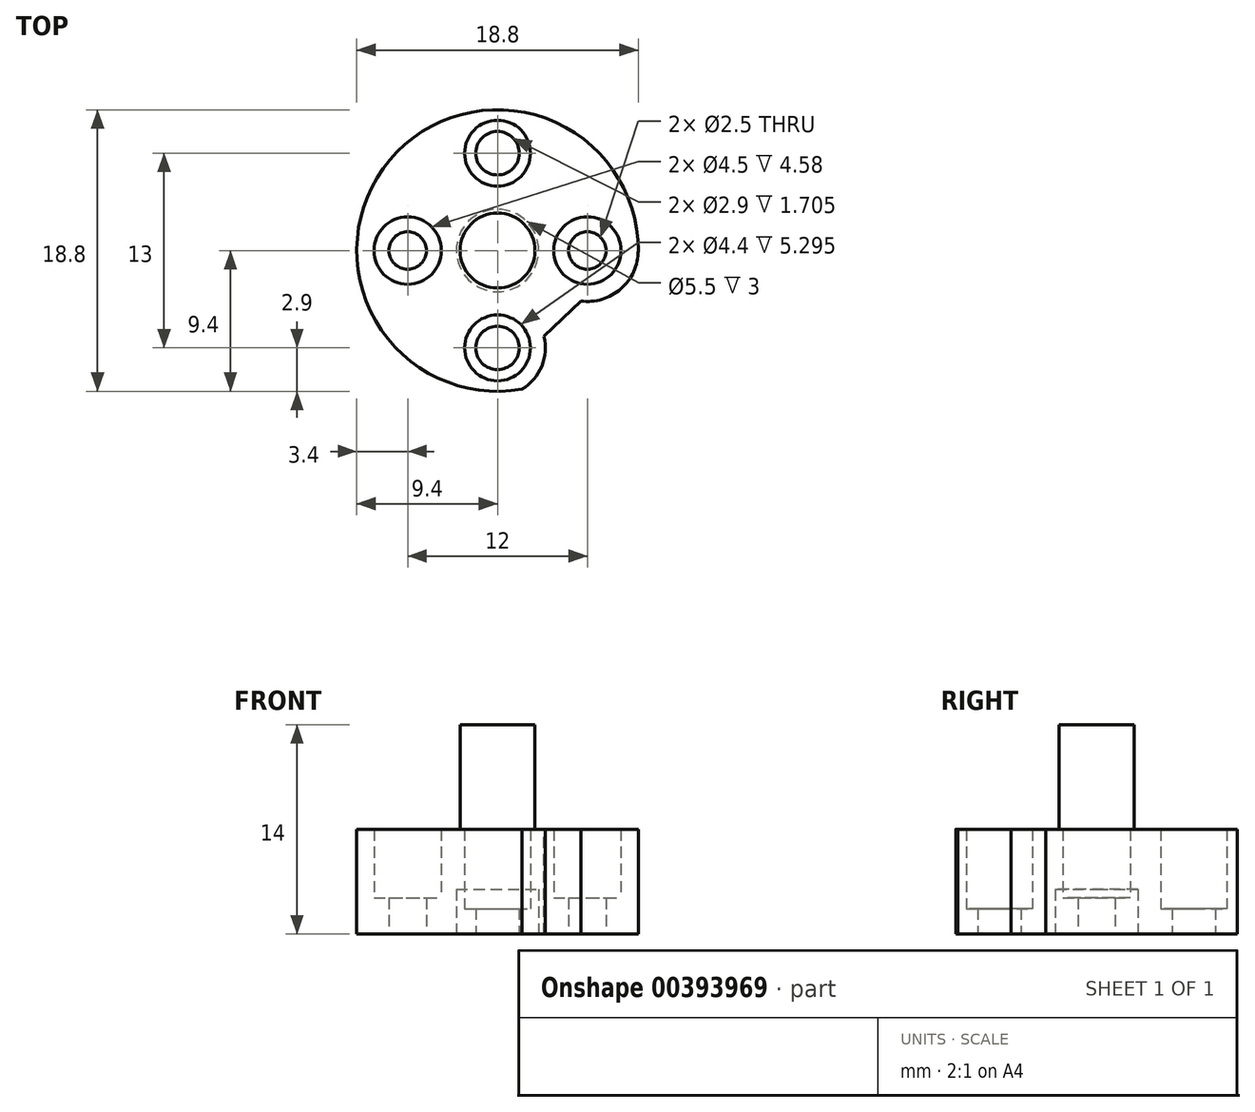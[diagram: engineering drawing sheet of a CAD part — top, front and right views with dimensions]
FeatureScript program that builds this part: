
annotation { "Feature Type Name" : "Feature", "Feature Type Description" : "" }
export const myFeature = defineFeature(function(context is Context, id is Id, definition is map)
    precondition{}
    {
        {
            var Q0;
            Q0=qCreatedBy(makeId("Top.planeOp"),FACE);
            var sketch = newSketch(context, id + "F0", { "sketchPlane" : qUnion([Q0])});
            skCircle(sketch, "E0", {"center": v(0, 0) * mm, "radius": 9.4 * mm});
            skSolve(sketch);
        }
        {
            var Q0;
            Q0 = qSketchRegion(id + "F0", true);
            extrude(context, id + "F1", {"entities" : qUnion([Q0]), "depth" : 7 * mm});
        }
        {
            var Q0;
            Q0=makeQuery(id+"F1.opExtrude","CAP_FACE",FACE,{"disambiguationData":[OSD([sQuery(id+"F0.wireOp",EDGE,"E0")])],"isStart":false});
            var sketch = newSketch(context, id + "F2", { "sketchPlane" : qUnion([Q0])});
            skCircle(sketch, "E1", {"center": v(0, 0) * mm, "radius": 2.5 * mm});
            skSolve(sketch);
        }
        {
            var Q0;
            Q0 = qSketchRegion(id + "F2", true);
            extrude(context, id + "F3", {"entities" : qUnion([Q0]), "operationType" : NewBodyOperationType.ADD, "depth" : 7 * mm});
        }
        {
            var Q0;
            Q0=makeQuery(id+"F1.opExtrude","CAP_FACE",FACE,{"disambiguationData":[OSD([sQuery(id+"F0.wireOp",EDGE,"E0")])],"isStart":true});
            var sketch = newSketch(context, id + "F4", { "sketchPlane" : qUnion([Q0])});
            skCircle(sketch, "E2", {"center": v(6, 0) * mm, "radius": 1.25 * mm});
            skLineSegment(sketch, "E3", {"start": v(0, 0) * mm, "end": v(6, 0) * mm, "construction": true});
            skCircle(sketch, "E4.MirrorC", {"center": v(-6, 0) * mm, "radius": 1.25 * mm});
            skSolve(sketch);
        }
        {
            var Q0;
            Q0 = qSketchRegion(id + "F4", true);
            extrude(context, id + "F5", {"entities" : qUnion([Q0]), "operationType" : NewBodyOperationType.REMOVE, "oppositeDirection" : true, "depth" : ((4.7 - 2.5) * 1.1) * mm});
        }
        {
            var Q0;
            Q0=makeQuery(id+"F5.boolean.opBoolean","COPY",FACE,{"derivedFrom":makeQuery(id+"F5.opExtrude","CAP_FACE",FACE,{"disambiguationData":[OSD([sQuery(id+"F4.wireOp",EDGE,"E4.MirrorC")])],"isStart":false})});
            var sketch = newSketch(context, id + "F6", { "sketchPlane" : qUnion([Q0])});
            skCircle(sketch, "E5", {"center": v(-6, 0) * mm, "radius": 2.25 * mm});
            skCircle(sketch, "E6.MirrorC", {"center": v(6, 0) * mm, "radius": 2.25 * mm});
            skSolve(sketch);
        }
        {
            var Q0;
            Q0 = qSketchRegion(id + "F6", true);
            var Q1;
            Q1=makeQuery(id+"F1.opExtrude","CAP_FACE",FACE,{"disambiguationData":[OSD([sQuery(id+"F0.wireOp",EDGE,"E0")])],"isStart":false});
            extrude(context, id + "F7", {"entities" : qUnion([Q0]), "operationType" : NewBodyOperationType.REMOVE, "endBound" : BoundingType.UP_TO_SURFACE, "oppositeDirection" : true, "endBoundEntityFace" : qUnion([Q1]), "depth" : 25 * mm});
        }
        {
            var Q0;
            Q0=makeQuery(id+"F1.opExtrude","CAP_FACE",FACE,{"disambiguationData":[OSD([sQuery(id+"F0.wireOp",EDGE,"E0")])],"isStart":true});
            var sketch = newSketch(context, id + "F8", { "sketchPlane" : qUnion([Q0])});
            skLineSegment(sketch, "E7", {"start": v(0, 0) * mm, "end": v(0, -6.5) * mm, "construction": true});
            skCircle(sketch, "E8", {"center": v(0, -6.5) * mm, "radius": 1.45 * mm});
            skCircle(sketch, "E9.MirrorC", {"center": v(0, 6.5) * mm, "radius": 1.45 * mm});
            skSolve(sketch);
        }
        {
            var Q0;
            Q0 = qSketchRegion(id + "F8", true);
            extrude(context, id + "F9", {"entities" : qUnion([Q0]), "operationType" : NewBodyOperationType.REMOVE, "oppositeDirection" : true, "depth" : ((3 - 1.45) * 1.1) * mm});
        }
        {
            var Q0;
            Q0=makeQuery(id+"F9.boolean.opBoolean","COPY",FACE,{"derivedFrom":makeQuery(id+"F9.opExtrude","CAP_FACE",FACE,{"disambiguationData":[OSD([sQuery(id+"F8.wireOp",EDGE,"E8")])],"isStart":false})});
            var sketch = newSketch(context, id + "F10", { "sketchPlane" : qUnion([Q0])});
            skCircle(sketch, "E10", {"center": v(0, -6.5) * mm, "radius": 2.2 * mm});
            skCircle(sketch, "E11.MirrorC", {"center": v(0, 6.5) * mm, "radius": 2.2 * mm});
            skSolve(sketch);
        }
        {
            var Q0;
            Q0 = qSketchRegion(id + "F10", true);
            var Q1;
            Q1=makeQuery(id+"F1.opExtrude","CAP_FACE",FACE,{"disambiguationData":[OSD([sQuery(id+"F0.wireOp",EDGE,"E0")])],"isStart":false});
            extrude(context, id + "F11", {"entities" : qUnion([Q0]), "operationType" : NewBodyOperationType.REMOVE, "endBound" : BoundingType.UP_TO_SURFACE, "oppositeDirection" : true, "endBoundEntityFace" : qUnion([Q1]), "depth" : 25 * mm});
        }
        {
            var Q0;
            Q0=makeQuery(id+"F1.opExtrude","CAP_FACE",FACE,{"disambiguationData":[OSD([sQuery(id+"F0.wireOp",EDGE,"E0")])],"isStart":true});
            var sketch = newSketch(context, id + "F12", { "sketchPlane" : qUnion([Q0])});
            skCircle(sketch, "E12", {"center": v(0, 0) * mm, "radius": 2.75 * mm});
            skSolve(sketch);
        }
        {
            var Q0;
            Q0 = qSketchRegion(id + "F12", true);
            extrude(context, id + "F13", {"entities" : qUnion([Q0]), "operationType" : NewBodyOperationType.REMOVE, "oppositeDirection" : true, "depth" : 3 * mm});
        }
        {
            var Q0;
            Q0=makeQuery(id+"F1.opExtrude","CAP_FACE",FACE,{"disambiguationData":[OSD([sQuery(id+"F0.wireOp",EDGE,"E0")])],"isStart":false});
            var sketch = newSketch(context, id + "F14", { "sketchPlane" : qUnion([Q0])});
            skCircle(sketch, "E13", {"center": v(0, 0) * mm, "radius": 6.5 * mm, "construction": true});
            skArc(sketch, "E14", {"start": v(1.62, -9.26) * mm, "mid": v(2.95, -7.73) * mm, "end": v(3.1, -5.71) * mm});
            skArc(sketch, "E15", {"start": v(5.56, -3.37) * mm, "mid": v(8.24, -2.56) * mm, "end": v(9.4, 0) * mm});
            skLineSegment(sketch, "E16", {"start": v(5.56, -3.37) * mm, "end": v(3.1, -5.71) * mm});
            skArc(sketch, "E17", {"start": v(1.62, -9.26) * mm, "mid": v(7.2, -6.05) * mm, "end": v(9.4, 0) * mm});
            skSolve(sketch);
        }
        {
            var Q0;
            Q0 = qSketchRegion(id + "F14", true);
            var Q1;
            Q1=makeQuery(id+"F1.opExtrude","CAP_FACE",FACE,{"disambiguationData":[OSD([sQuery(id+"F0.wireOp",EDGE,"E0")])],"isStart":true});
            extrude(context, id + "F15", {"entities" : qUnion([Q0]), "operationType" : NewBodyOperationType.REMOVE, "endBound" : BoundingType.UP_TO_SURFACE, "oppositeDirection" : true, "endBoundEntityFace" : qUnion([Q1]), "depth" : 25 * mm});
        }
    });
